# Revit family: Eurolan_Комплект профилей опорных L-типа до 150 кг
name_source: partatom
category: Устройства связи
units: mm (PartAtom-declared; Revit-internal decimal feet)

## family parameters
Всегда вертикально = Да
На основе рабочей плоскости = Нет
Общий = Нет
При загрузке вырезать с полостями = Нет
Размер круглого соединителя = Использовать диаметр
Сохранять ориентацию аннотаций = Нет
Тип детали = Нормальный
Точка расчета площади = Нет

## types (4) — shared parameters
ADSK_Единица измерения = шт
ADSK_Завод-изготовитель = Eurolan
ADSK_Количество = 1
ADSK_Марка = L-типа
ADSK_Материал = Оценковка
ADSK_Наименование краткое = Комплект профилей опорных L-типа

## per-type parameters (varying)
| type | ADSK_Код изделия | ADSK_Масса | ADSK_Наименование | Выбор_графики | Длина |
| Комплект профилей опорных L-типа 450 мм | 60A-41-45-11SL | 1.4 | Комплект профилей опорных L-типа 450 мм, до 150 кг | Комплект профилей опорных L-типа_435 : 435 | 435 мм |
| Комплект профилей опорных L-типа 580 мм | 60A-41-58-11SL | 1.8 | Комплект профилей опорных L-типа 580 мм, до 150 кг | Комплект профилей опорных L-типа_565 : 565 | 565 мм |
| Комплект профилей опорных L-типа 750 мм | 60A-41-75-11SL | 2.4 | Комплект профилей опорных L-типа 750 мм, до 150 кг | Комплект профилей опорных L-типа_735 : 735 | 565 мм |
| Комплект профилей опорных L-типа 1000 мм | 60A-41-1A-11SL | 3.2 | Комплект профилей опорных L-типа 1000 мм, до 150 кг | Комплект профилей опорных L-типа_985 : 985 | 985 мм |
